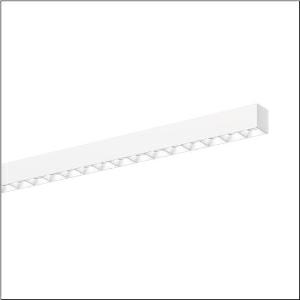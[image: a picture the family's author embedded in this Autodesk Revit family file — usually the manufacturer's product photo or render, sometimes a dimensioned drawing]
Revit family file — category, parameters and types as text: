
# Revit family: silica_r__21_51mx26dc3awb_8cf9
name_source: partatom
category: Lighting Fixtures
units: mm (PartAtom-declared; Revit-internal decimal feet)

## family parameters
Cut with Voids When Loaded = No
Host = Face
Light Source = No
Part Type = Normal
Room Calculation Point = No
Round Connector Dimension = Use Diameter
Shared = No

## types (1)
- --- (1 x LED, 10800 lm, 63.6 W, 3000K)
    Apparent Load = 64 VA
    CIE Flux Codes = 83 98 100 100 100
    Color Rendering = 80
    Color Temperature = 3000K
    Default Elevation = 1800 mm
    Description = Silica® 21, office luminaire, primary light control with darklight reflector, of PMMA, white, CAT 2 (L<= 3000cd/m²), light emission: direct distribution, primary light characteristic: symmetric, installation type: surface-mounted, LED, rated luminous flux: 10.800lm, luminous efficacy: 170lm/W, light colour: 830, colour temperature: 3000K, with terminal, 3+2-pole, max. 2.5mm², mains connection: 220..240V, AC, 50/60Hz, rated input power: 63.6W, luminaire housing, of aluminium, traffic white (RAL 9016), length: 3.004mm, width: 53mm, height: 53mm, protection rating (complete): IP20, insulation class (complete): insulation class I (protective earthing), certification: CE, permissible operating ambient temperature: 0..+35°C, standard: EN 50419, packaging unit: 1 piece
    Height = 0 mm  [stored 0 ft]
    Lamp = 1 x LED
    Lamp Light Flux = 10800 lm
    Lamp Power = 63.6 W
    Lamp count = 1
    Length = 3004 mm
    Luminous efficacy = 170 lm/W
    Manufacturer = Siteco
    ModVariant = No
    Model = 51MX26DC3AWB
    Mounting Place = Ceiling
    Mounting Type = Recessed
    Number of Poles = 1
    OnlyDefault = Yes
    Power Factor = 1
    Product Name = Silica® 21
    Product group = office luminaire | ceiling recessed
    ProductGroupID = 401
    Protection Class = Protection class I
    Protection Degree = IP 20
    RLX_Detail_Level = 1
    RLX_Emergency_Light_Flux = 0 lm
    RLX_Emergency_Type = 0
    RLX_Emergency_Type_DB = No
    RlxData = <blob elided: 59481 chars, md5=1c24e2b2>
    Socket = socket
    Standby Power = 0 W
    System Light Flux = 10800 lm
    System Power = 64 W
    Type Comments = factory setting: luminous flux: 100 % | dim-lin: 254 | 360 mA
    Type Image = l_1297772.jpg
    URL = http://relux.com
    VarID = @adj_055283
    Voltage = 0 V
    Weight = 0.00 kg
    Width = 53 mm

note: [stored X ft] marks values corroborated as IEEE doubles in the binary element streams (Revit-internal decimal feet)

## geometry (parser evidence)
native form markers: Blend x4, Sweep x13
no freeform markers — native parametric forms only
